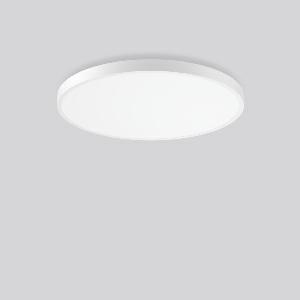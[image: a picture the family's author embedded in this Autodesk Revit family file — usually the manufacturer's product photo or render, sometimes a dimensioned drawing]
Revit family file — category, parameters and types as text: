
# Revit family: triona_round_a_312387_002_2_730_735a
name_source: partatom
category: Lighting Fixtures
units: mm (PartAtom-declared; Revit-internal decimal feet)

## family parameters
Cut with Voids When Loaded = No
Host = Face
Light Source = No
Part Type = Normal
Room Calculation Point = No
Round Connector Dimension = Use Diameter
Shared = No

## types (1)
- TuneableWhite 846 (1 x LED Modul 846, 4800 lm, 4600)
    Apparent Load = 49 VA
    CIE Flux Codes = 50 80 96 100 100
    Color Rendering = 80
    Color Temperature = 4600
    Default Elevation = 1800 mm
    Description = Series: TRIONA round
Decorative round LED surface-mounted luminaire. Flat, seamless frame: aluminium extrusion profile, powder coated. Cover made of sheet steel, powder-coated. Light emission through a diffuser: plastic, opal. Lightguide and diffuser made of non-yellowing plastic (PMMA). Lateral light emission (RZB SIDELITE technology) for above-average homogeneous light distribution. Tunable white versions, dynamically adjustable from 2700 K to 6500 K. Suitable for Ceiling mounting, Wall (surface). Tool-free mounting via bayonet connection. Electronic ballast included. Very easy installation thanks to Plug+Play connection. With Casambi smart+free Bluetooth control for wireless network and operation using Android / iOS devices, free app available for download. Ideal for use as part of the Human Centric Lighting concept in connection with RZB light management systems. 
Colour: traffic white, matt (RAL 9016)
Diameter: 845 mm
Height: 88 mm
Lamp: LED
Socket: without socket
Colour temperature: 2700K - 6500K
Colour rendering index (CRI): 80
System power: 49 W
Rated luminous flux: 4800 lm
Luminous efficiency: 98 lm/W
System power 2: 51 W
Rated luminous flux 2: 4550 lm
Luminous efficiency 2: 89 lm/W
System power 3: 51 W
Rated luminous flux 3: 4650 lm
Luminous efficiency 3: 91 lm/W
Control gear: Dimmable Bluetooth converter
Protection class: I
Type of protection: IP 20
    Height = 88 mm
    Lamp = 1 x LED Modul 846
    Lamp Light Flux = 4800 lm
    Lamp count = 1
    Length = 845 mm
    Lifetime = 50000 h
    Luminous efficacy = 98 lm/W
    Manufacturer = RZB
    ModVariant = No
    Model = 312387.002.2.730
    Mounting Place = Ceiling
    Mounting Type = Surface mounted
    Number of Poles = 1
    OnlyDefault = Yes
    Power Factor = 1
    Product Name = TRIONA round A
    Product group = Surface mounted modular luminaires
    ProductGroupID = 306
    Protection Class = Protection class I
    Protection Degree = IP 20
    RLX_Detail_Level = 1
    RLX_Emergency_Light_Flux = 0 lm
    RLX_Emergency_Type = 0
    RLX_Emergency_Type_DB = No
    RlxData = <blob elided: 33317 chars, md5=92df899a>
    Socket = socket
    Standby Power = 0 W
    System Light Flux = 4800 lm
    System Power = 49 W
    Type Comments = TuneableWhite 846
    Type Image = 312388.002.jpg
    URL = http://relux.com
    VarID = tuneablewhite_846
    Voltage = 230 V
    Voltage Range = 220-240 V
    Weight = 0.00 kg
    Width = 0 mm  [stored 0 ft]

note: [stored X ft] marks values corroborated as IEEE doubles in the binary element streams (Revit-internal decimal feet)

## geometry (parser evidence)
native form markers: Blend x4, Sweep x9
no freeform markers — native parametric forms only
